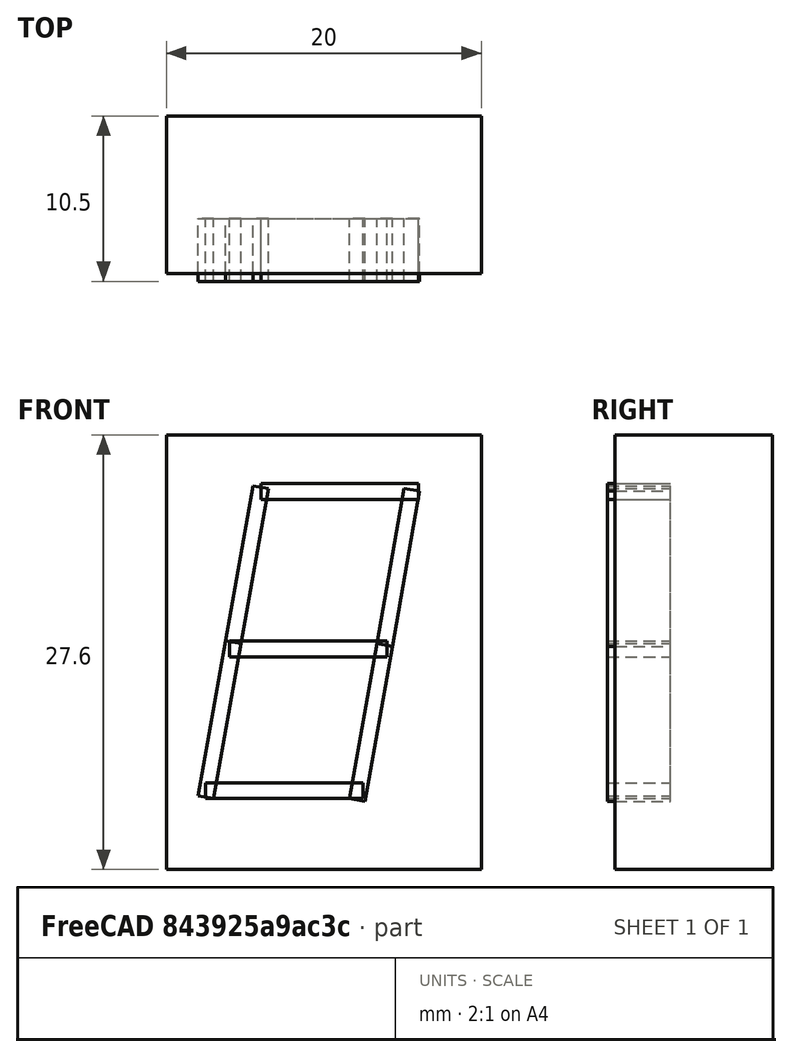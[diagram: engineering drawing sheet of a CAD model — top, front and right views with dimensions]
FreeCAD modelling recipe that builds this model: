
FCSTD DOCUMENT  (FreeCAD 0.21R33668 +26 (Git))
Label: RGB-7seg
License: All rights reserved
LicenseURL: http://en.wikipedia.org/wiki/All_rights_reserved
objects: Part::Box×8
note: 8 computed .brp shape members not serialized (recipe doc carries the construction recipe); baked Part::Feature solids carry a one-line shape summary decoded from their .brp

FEATURE [Part::Box] Box  label="Cube"
  AttacherType = Attacher::AttachEngine3D
  Height = 27.6
  Length = 20
  Placement = pos=(2,0,0) rot=(0,0,1;0rad)
  Width = 10
FEATURE [Part::Box] Box001  label="Cube001"
  AttacherType = Attacher::AttachEngine3D
  Height = 1
  Length = 10
  Placement = pos=(4.5,-0.5,4.5) rot=(0,0,1;0rad)
  Width = 4
FEATURE [Part::Box] Box002  label="Cube002"
  AttacherType = Attacher::AttachEngine3D
  Height = 1
  Length = 10
  Placement = pos=(6,-0.5,13.5) rot=(0,0,1;0rad)
  Width = 4
FEATURE [Part::Box] Box003  label="Cube003"
  AttacherType = Attacher::AttachEngine3D
  Height = 1
  Length = 10
  Placement = pos=(8,-0.5,23.5) rot=(0,0,1;0rad)
  Width = 4
FEATURE [Part::Box] Box004  label="Cube004"
  AttacherType = Attacher::AttachEngine3D
  Height = 1
  Length = 10
  Placement = pos=(5,-0.5,4.5) rot=(0,1,0;4.88692rad)
  Width = 4
FEATURE [Part::Box] Box005  label="Cube005"
  AttacherType = Attacher::AttachEngine3D
  Height = 1
  Length = 10
  Placement = pos=(14.6161,-0.5,4.32755) rot=(0,1,0;4.88692rad)
  Width = 4
FEATURE [Part::Box] Box006  label="Cube006"
  AttacherType = Attacher::AttachEngine3D
  Height = 1
  Length = 10
  Placement = pos=(6.73648,-0.5,14.3481) rot=(0,1,0;4.88692rad)
  Width = 4
FEATURE [Part::Box] Box007  label="Cube007"
  AttacherType = Attacher::AttachEngine3D
  Height = 1
  Length = 10
  Placement = pos=(16.3526,-0.5,14.1756) rot=(0,1,0;4.88692rad)
  Width = 4
